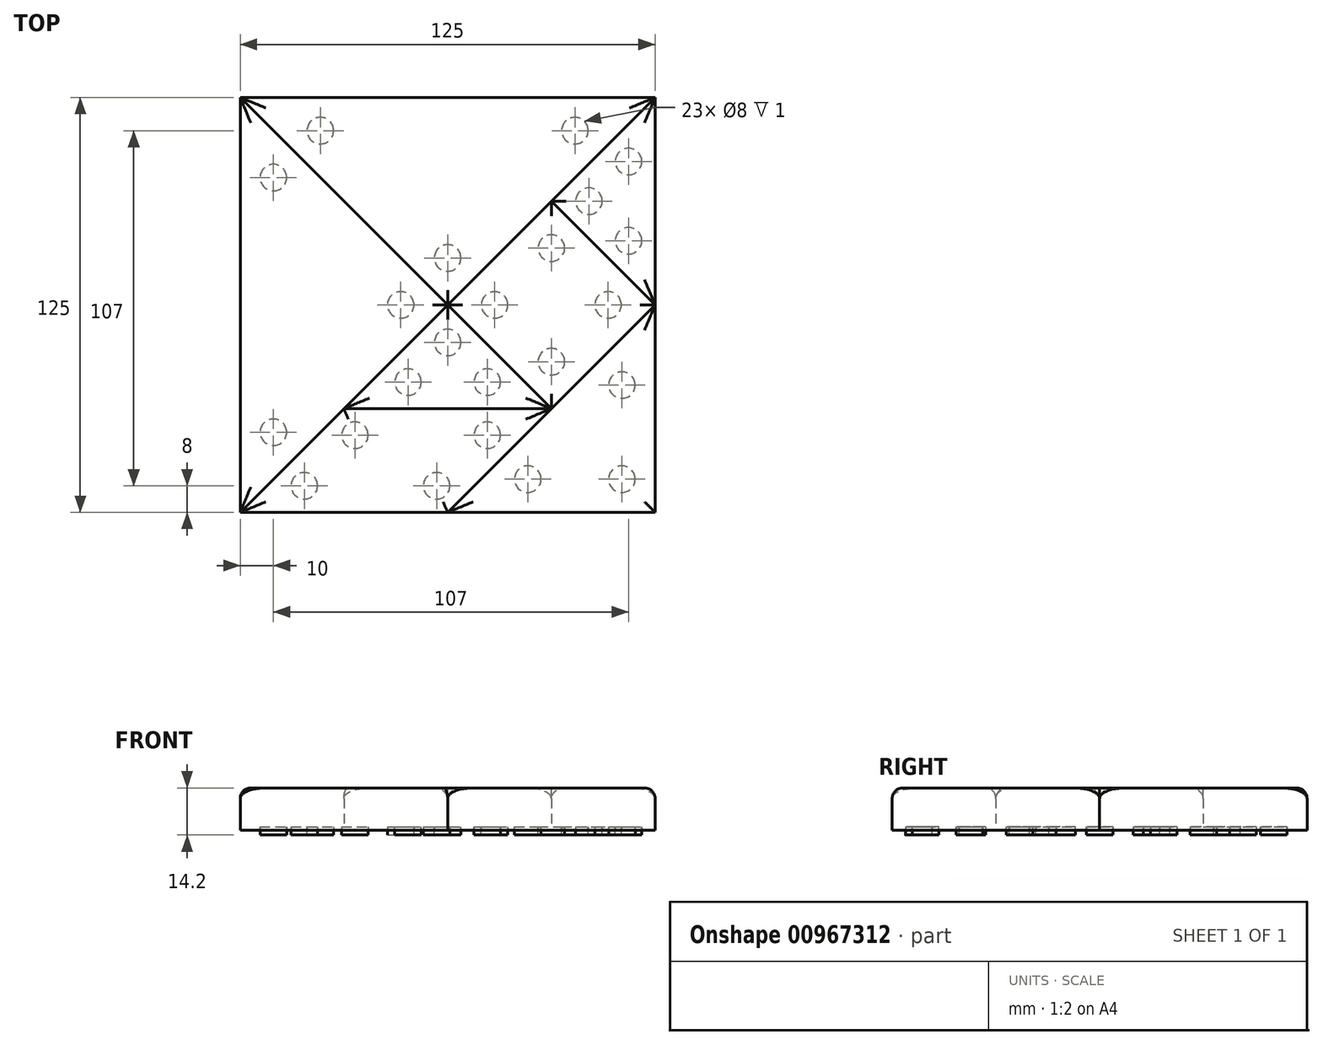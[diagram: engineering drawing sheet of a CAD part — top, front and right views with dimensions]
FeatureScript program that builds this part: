
annotation { "Feature Type Name" : "Feature", "Feature Type Description" : "" }
export const myFeature = defineFeature(function(context is Context, id is Id, definition is map)
    precondition{}
    {
        {
            var Q0;
            Q0=qCreatedBy(makeId("Top.planeOp"),FACE);
            var sketch = newSketch(context, id + "F0", { "sketchPlane" : qUnion([Q0])});
            skLineSegment(sketch, "E0.bottom", {"start": v(62.5, -62.5) * mm, "end": v(-62.5, -62.5) * mm});
            skLineSegment(sketch, "E0.top", {"start": v(62.5, 62.5) * mm, "end": v(-62.5, 62.5) * mm});
            skLineSegment(sketch, "E0.left", {"start": v(62.5, -62.5) * mm, "end": v(62.5, 62.5) * mm});
            skLineSegment(sketch, "E0.right", {"start": v(-62.5, -62.5) * mm, "end": v(-62.5, 62.5) * mm});
            skPoint(sketch, "E0.middle", {"position": v(0, 0) * mm});
            skLineSegment(sketch, "E1", {"start": v(62.5, 62.5) * mm, "end": v(-62.5, -62.5) * mm});
            skLineSegment(sketch, "E2", {"start": v(0, -62.5) * mm, "end": v(62.5, 0) * mm});
            skLineSegment(sketch, "E3", {"start": v(0, 0) * mm, "end": v(31.25, -31.25) * mm});
            skLineSegment(sketch, "E4", {"start": v(62.5, 0) * mm, "end": v(31.25, 31.25) * mm});
            skLineSegment(sketch, "E5", {"start": v(31.25, -31.25) * mm, "end": v(-31.25, -31.25) * mm});
            skLineSegment(sketch, "E6", {"start": v(0, 0) * mm, "end": v(-62.5, 62.5) * mm});
            skSolve(sketch);
        }
        {
            var Q0;
            {var subQ0=sQuery(id+"F0.wireOp",EDGE,"E0.right");Q0=makeQuery(id+"F0.imprint","IMPRINT",FACE,{"disambiguationData":[TD([[makeQuery(id+"F0.imprint","IMPRINT",EDGE,{"derivedFrom":subQ0}),-1.0]])]});}
            extrude(context, id + "F1", {"entities" : qUnion([Q0]), "depth" : 12.7 * mm, "offsetDistance" : 25.4 * mm});
        }
        {
            var Q0;
            {var subQ0=sQuery(id+"F0.wireOp",EDGE,"E0.top");Q0=makeQuery(id+"F0.imprint","IMPRINT",FACE,{"disambiguationData":[TD([[makeQuery(id+"F0.imprint","IMPRINT",EDGE,{"derivedFrom":subQ0}),1.0]])]});}
            extrude(context, id + "F2", {"entities" : qUnion([Q0]), "depth" : 12.7 * mm, "offsetDistance" : 25.4 * mm});
        }
        {
            var Q0;
            {var subQ5=sQuery(id+"F0.wireOp",EDGE,"E5");Q0=makeQuery(id+"F0.imprint","IMPRINT",FACE,{"disambiguationData":[TD([[makeQuery(id+"F0.imprint","IMPRINT",EDGE,{"derivedFrom":subQ5}),1.0]])]});}
            extrude(context, id + "F3", {"entities" : qUnion([Q0]), "depth" : 12.7 * mm, "offsetDistance" : 25.4 * mm});
        }
        {
            var Q0;
            {var subQ0=sQuery(id+"F0.wireOp",EDGE,"E3");Q0=makeQuery(id+"F0.imprint","IMPRINT",FACE,{"disambiguationData":[TD([[makeQuery(id+"F0.imprint","IMPRINT",EDGE,{"derivedFrom":subQ0}),-1.0]])]});}
            extrude(context, id + "F4", {"entities" : qUnion([Q0]), "depth" : 12.7 * mm, "offsetDistance" : 25.4 * mm});
        }
        {
            var Q0;
            {var subQ0=sQuery(id+"F0.wireOp",EDGE,"E3");Q0=makeQuery(id+"F0.imprint","IMPRINT",FACE,{"disambiguationData":[TD([[makeQuery(id+"F0.imprint","IMPRINT",EDGE,{"derivedFrom":subQ0}),1.0]])]});}
            extrude(context, id + "F5", {"entities" : qUnion([Q0]), "depth" : 12.7 * mm, "offsetDistance" : 25.4 * mm});
        }
        {
            var Q0;
            {var subQ0=sQuery(id+"F0.wireOp",EDGE,"E0.left");var subQ1=sQuery(id+"F0.wireOp",EDGE,"E0.bottom");var subQ2=makeQuery(id+"F0.imprint","INTERSECT",VERTEX,{"derivedFrom":[subQ1,subQ0]});Q0=makeQuery(id+"F0.imprint","IMPRINT",FACE,{"disambiguationData":[TD([[makeQuery(id+"F0.imprint","IMPRINT",EDGE,{"disambiguationData":[TD([[subQ2,-1.0]])],"derivedFrom":subQ1}),-1.0]])]});}
            extrude(context, id + "F6", {"entities" : qUnion([Q0]), "depth" : 12.7 * mm, "offsetDistance" : 25.4 * mm});
        }
        {
            var Q0;
            {var subQ3=sQuery(id+"F0.wireOp",EDGE,"E4");Q0=makeQuery(id+"F0.imprint","IMPRINT",FACE,{"disambiguationData":[TD([[makeQuery(id+"F0.imprint","IMPRINT",EDGE,{"derivedFrom":subQ3}),-1.0]])]});}
            extrude(context, id + "F7", {"entities" : qUnion([Q0]), "depth" : 12.7 * mm, "offsetDistance" : 25.4 * mm});
        }
        {
            var Q0;
            Q0=makeQuery(id+"F1.opExtrude","CAP_FACE",FACE,{"disambiguationData":[OSD([sQuery(id+"F0.wireOp",EDGE,"E0.right"),sQuery(id+"F0.wireOp",EDGE,"E1"),sQuery(id+"F0.wireOp",EDGE,"E6")])],"isStart":false});
            var Q1;
            Q1=makeQuery(id+"F2.opExtrude","CAP_FACE",FACE,{"disambiguationData":[OSD([sQuery(id+"F0.wireOp",EDGE,"E0.top"),sQuery(id+"F0.wireOp",EDGE,"E1"),sQuery(id+"F0.wireOp",EDGE,"E6")])],"isStart":false});
            var Q2;
            Q2=makeQuery(id+"F3.opExtrude","CAP_FACE",FACE,{"disambiguationData":[OSD([sQuery(id+"F0.wireOp",EDGE,"E0.bottom"),sQuery(id+"F0.wireOp",EDGE,"E1"),sQuery(id+"F0.wireOp",EDGE,"E2"),sQuery(id+"F0.wireOp",EDGE,"E5")])],"isStart":false});
            var Q3;
            Q3=makeQuery(id+"F4.opExtrude","CAP_FACE",FACE,{"disambiguationData":[OSD([sQuery(id+"F0.wireOp",EDGE,"E1"),sQuery(id+"F0.wireOp",EDGE,"E3"),sQuery(id+"F0.wireOp",EDGE,"E5")])],"isStart":false});
            var Q4;
            Q4=makeQuery(id+"F6.opExtrude","CAP_FACE",FACE,{"disambiguationData":[OSD([sQuery(id+"F0.wireOp",EDGE,"E0.bottom"),sQuery(id+"F0.wireOp",EDGE,"E0.left"),sQuery(id+"F0.wireOp",EDGE,"E2")])],"isStart":false});
            var Q5;
            Q5=makeQuery(id+"F5.opExtrude","CAP_FACE",FACE,{"disambiguationData":[OSD([sQuery(id+"F0.wireOp",EDGE,"E1"),sQuery(id+"F0.wireOp",EDGE,"E2"),sQuery(id+"F0.wireOp",EDGE,"E3"),sQuery(id+"F0.wireOp",EDGE,"E4")])],"isStart":false});
            var Q6;
            Q6=makeQuery(id+"F7.opExtrude","CAP_FACE",FACE,{"disambiguationData":[OSD([sQuery(id+"F0.wireOp",EDGE,"E0.left"),sQuery(id+"F0.wireOp",EDGE,"E1"),sQuery(id+"F0.wireOp",EDGE,"E4")])],"isStart":false});
            fillet(context, id + "F8", {"entities" : qUnion([Q0, Q1, Q2, Q3, Q4, Q5, Q6]), "radius" : 3.17 * mm, "tangentPropagation" : true, "allowEdgeOverflow" : false});
        }
        {
            var Q0;
            Q0=makeQuery(id+"F2.opExtrude","CAP_FACE",FACE,{"disambiguationData":[OSD([sQuery(id+"F0.wireOp",EDGE,"E0.top"),sQuery(id+"F0.wireOp",EDGE,"E1"),sQuery(id+"F0.wireOp",EDGE,"E6")])],"isStart":true});
            var sketch = newSketch(context, id + "F9", { "sketchPlane" : qUnion([Q0])});
            skCircle(sketch, "E7", {"center": v(0, -14.14) * mm, "radius": 4 * mm});
            skCircle(sketch, "E8", {"center": v(38.36, -52.5) * mm, "radius": 4 * mm});
            skCircle(sketch, "E9", {"center": v(-38.36, -52.5) * mm, "radius": 4 * mm});
            skSolve(sketch);
        }
        {
            var Q0;
            Q0=makeQuery(id+"F5.opExtrude","CAP_FACE",FACE,{"disambiguationData":[OSD([sQuery(id+"F0.wireOp",EDGE,"E1"),sQuery(id+"F0.wireOp",EDGE,"E2"),sQuery(id+"F0.wireOp",EDGE,"E3"),sQuery(id+"F0.wireOp",EDGE,"E4")])],"isStart":true});
            var sketch = newSketch(context, id + "F10", { "sketchPlane" : qUnion([Q0])});
            skCircle(sketch, "E10", {"center": v(48.36, 0) * mm, "radius": 4 * mm});
            skCircle(sketch, "E11", {"center": v(14.14, 0) * mm, "radius": 4 * mm});
            skCircle(sketch, "E12", {"center": v(31.25, 17.1) * mm, "radius": 4 * mm});
            skCircle(sketch, "E13", {"center": v(31.25, -17.1) * mm, "radius": 4 * mm});
            skSolve(sketch);
        }
        {
            var Q0;
            Q0=makeQuery(id+"F4.opExtrude","CAP_FACE",FACE,{"disambiguationData":[OSD([sQuery(id+"F0.wireOp",EDGE,"E1"),sQuery(id+"F0.wireOp",EDGE,"E3"),sQuery(id+"F0.wireOp",EDGE,"E5")])],"isStart":true});
            var sketch = newSketch(context, id + "F11", { "sketchPlane" : qUnion([Q0])});
            skCircle(sketch, "E14", {"center": v(0, 11.31) * mm, "radius": 4 * mm});
            skCircle(sketch, "E15", {"center": v(11.94, 23.25) * mm, "radius": 4 * mm});
            skCircle(sketch, "E16", {"center": v(-11.94, 23.25) * mm, "radius": 4 * mm});
            skSolve(sketch);
        }
        {
            var Q0;
            Q0=makeQuery(id+"F1.opExtrude","CAP_FACE",FACE,{"disambiguationData":[OSD([sQuery(id+"F0.wireOp",EDGE,"E0.right"),sQuery(id+"F0.wireOp",EDGE,"E1"),sQuery(id+"F0.wireOp",EDGE,"E6")])],"isStart":true});
            var sketch = newSketch(context, id + "F12", { "sketchPlane" : qUnion([Q0])});
            skCircle(sketch, "E17", {"center": v(-14.14, 0) * mm, "radius": 4 * mm});
            skCircle(sketch, "E18", {"center": v(-52.5, -38.36) * mm, "radius": 4 * mm});
            skCircle(sketch, "E19", {"center": v(-52.5, 38.36) * mm, "radius": 4 * mm});
            skSolve(sketch);
        }
        {
            var Q0;
            Q0=makeQuery(id+"F6.opExtrude","CAP_FACE",FACE,{"disambiguationData":[OSD([sQuery(id+"F0.wireOp",EDGE,"E0.bottom"),sQuery(id+"F0.wireOp",EDGE,"E0.left"),sQuery(id+"F0.wireOp",EDGE,"E2")])],"isStart":true});
            var sketch = newSketch(context, id + "F13", { "sketchPlane" : qUnion([Q0])});
            skCircle(sketch, "E20", {"center": v(52.5, 52.5) * mm, "radius": 4 * mm});
            skCircle(sketch, "E21", {"center": v(52.5, 24.14) * mm, "radius": 4 * mm});
            skCircle(sketch, "E22", {"center": v(24.14, 52.5) * mm, "radius": 4 * mm});
            skSolve(sketch);
        }
        {
            var Q0;
            Q0=makeQuery(id+"F3.opExtrude","CAP_FACE",FACE,{"disambiguationData":[OSD([sQuery(id+"F0.wireOp",EDGE,"E0.bottom"),sQuery(id+"F0.wireOp",EDGE,"E1"),sQuery(id+"F0.wireOp",EDGE,"E2"),sQuery(id+"F0.wireOp",EDGE,"E5")])],"isStart":true});
            var sketch = newSketch(context, id + "F14", { "sketchPlane" : qUnion([Q0])});
            skCircle(sketch, "E23", {"center": v(-3.31, 54.5) * mm, "radius": 4 * mm});
            skCircle(sketch, "E24", {"center": v(11.94, 39.25) * mm, "radius": 4 * mm});
            skCircle(sketch, "E25", {"center": v(-27.94, 39.25) * mm, "radius": 4 * mm});
            skCircle(sketch, "E26", {"center": v(-43.19, 54.5) * mm, "radius": 4 * mm});
            skSolve(sketch);
        }
        {
            var Q0;
            Q0=makeQuery(id+"F7.opExtrude","CAP_FACE",FACE,{"disambiguationData":[OSD([sQuery(id+"F0.wireOp",EDGE,"E0.left"),sQuery(id+"F0.wireOp",EDGE,"E1"),sQuery(id+"F0.wireOp",EDGE,"E4")])],"isStart":true});
            var sketch = newSketch(context, id + "F15", { "sketchPlane" : qUnion([Q0])});
            skCircle(sketch, "E27", {"center": v(54.5, -19.31) * mm, "radius": 4 * mm});
            skCircle(sketch, "E28", {"center": v(42.56, -31.25) * mm, "radius": 4 * mm});
            skCircle(sketch, "E29", {"center": v(54.5, -43.19) * mm, "radius": 4 * mm});
            skSolve(sketch);
        }
        {
            var Q0;
            Q0=makeQuery(id+"F12.imprint","IMPRINT",FACE,{"disambiguationData":[TD([[makeQuery(id+"F12.imprint","IMPRINT",EDGE,{"derivedFrom":sQuery(id+"F12.wireOp",EDGE,"E19")}),1.0]])]});
            var Q1;
            Q1=makeQuery(id+"F12.imprint","IMPRINT",FACE,{"disambiguationData":[TD([[makeQuery(id+"F12.imprint","IMPRINT",EDGE,{"derivedFrom":sQuery(id+"F12.wireOp",EDGE,"E17")}),1.0]])]});
            var Q2;
            Q2=makeQuery(id+"F12.imprint","IMPRINT",FACE,{"disambiguationData":[TD([[makeQuery(id+"F12.imprint","IMPRINT",EDGE,{"derivedFrom":sQuery(id+"F12.wireOp",EDGE,"E18")}),1.0]])]});
            extrude(context, id + "F16", {"entities" : qUnion([Q0, Q1, Q2]), "operationType" : NewBodyOperationType.REMOVE, "oppositeDirection" : true, "depth" : 1 * mm, "offsetDistance" : 25 * mm});
        }
        {
            var Q0;
            Q0=makeQuery(id+"F9.imprint","IMPRINT",FACE,{"disambiguationData":[TD([[makeQuery(id+"F9.imprint","IMPRINT",EDGE,{"derivedFrom":sQuery(id+"F9.wireOp",EDGE,"E7")}),1.0]])]});
            var Q1;
            Q1=makeQuery(id+"F9.imprint","IMPRINT",FACE,{"disambiguationData":[TD([[makeQuery(id+"F9.imprint","IMPRINT",EDGE,{"derivedFrom":sQuery(id+"F9.wireOp",EDGE,"E9")}),1.0]])]});
            var Q2;
            Q2=makeQuery(id+"F9.imprint","IMPRINT",FACE,{"disambiguationData":[TD([[makeQuery(id+"F9.imprint","IMPRINT",EDGE,{"derivedFrom":sQuery(id+"F9.wireOp",EDGE,"E8")}),1.0]])]});
            extrude(context, id + "F17", {"entities" : qUnion([Q0, Q1, Q2]), "operationType" : NewBodyOperationType.REMOVE, "oppositeDirection" : true, "depth" : 1 * mm, "offsetDistance" : 25 * mm});
        }
        {
            var Q0;
            Q0=makeQuery(id+"F15.imprint","IMPRINT",FACE,{"disambiguationData":[TD([[makeQuery(id+"F15.imprint","IMPRINT",EDGE,{"derivedFrom":sQuery(id+"F15.wireOp",EDGE,"E28")}),1.0]])]});
            var Q1;
            Q1=makeQuery(id+"F15.imprint","IMPRINT",FACE,{"disambiguationData":[TD([[makeQuery(id+"F15.imprint","IMPRINT",EDGE,{"derivedFrom":sQuery(id+"F15.wireOp",EDGE,"E27")}),1.0]])]});
            var Q2;
            Q2=makeQuery(id+"F15.imprint","IMPRINT",FACE,{"disambiguationData":[TD([[makeQuery(id+"F15.imprint","IMPRINT",EDGE,{"derivedFrom":sQuery(id+"F15.wireOp",EDGE,"E29")}),1.0]])]});
            extrude(context, id + "F18", {"entities" : qUnion([Q0, Q1, Q2]), "operationType" : NewBodyOperationType.REMOVE, "oppositeDirection" : true, "depth" : 1 * mm, "offsetDistance" : 25 * mm});
        }
        {
            var Q0;
            Q0=makeQuery(id+"F10.imprint","IMPRINT",FACE,{"disambiguationData":[TD([[makeQuery(id+"F10.imprint","IMPRINT",EDGE,{"derivedFrom":sQuery(id+"F10.wireOp",EDGE,"E11")}),1.0]])]});
            var Q1;
            Q1=makeQuery(id+"F10.imprint","IMPRINT",FACE,{"disambiguationData":[TD([[makeQuery(id+"F10.imprint","IMPRINT",EDGE,{"derivedFrom":sQuery(id+"F10.wireOp",EDGE,"E12")}),1.0]])]});
            var Q2;
            Q2=makeQuery(id+"F10.imprint","IMPRINT",FACE,{"disambiguationData":[TD([[makeQuery(id+"F10.imprint","IMPRINT",EDGE,{"derivedFrom":sQuery(id+"F10.wireOp",EDGE,"E10")}),1.0]])]});
            var Q3;
            Q3=makeQuery(id+"F10.imprint","IMPRINT",FACE,{"disambiguationData":[TD([[makeQuery(id+"F10.imprint","IMPRINT",EDGE,{"derivedFrom":sQuery(id+"F10.wireOp",EDGE,"E13")}),1.0]])]});
            extrude(context, id + "F19", {"entities" : qUnion([Q0, Q1, Q2, Q3]), "operationType" : NewBodyOperationType.REMOVE, "oppositeDirection" : true, "depth" : 1 * mm, "offsetDistance" : 25 * mm});
        }
        {
            var Q0;
            Q0=makeQuery(id+"F11.imprint","IMPRINT",FACE,{"disambiguationData":[TD([[makeQuery(id+"F11.imprint","IMPRINT",EDGE,{"derivedFrom":sQuery(id+"F11.wireOp",EDGE,"E16")}),1.0]])]});
            var Q1;
            Q1=makeQuery(id+"F11.imprint","IMPRINT",FACE,{"disambiguationData":[TD([[makeQuery(id+"F11.imprint","IMPRINT",EDGE,{"derivedFrom":sQuery(id+"F11.wireOp",EDGE,"E14")}),1.0]])]});
            var Q2;
            Q2=makeQuery(id+"F11.imprint","IMPRINT",FACE,{"disambiguationData":[TD([[makeQuery(id+"F11.imprint","IMPRINT",EDGE,{"derivedFrom":sQuery(id+"F11.wireOp",EDGE,"E15")}),1.0]])]});
            extrude(context, id + "F20", {"entities" : qUnion([Q0, Q1, Q2]), "operationType" : NewBodyOperationType.REMOVE, "oppositeDirection" : true, "depth" : 1 * mm, "offsetDistance" : 25 * mm});
        }
        {
            var Q0;
            Q0=makeQuery(id+"F14.imprint","IMPRINT",FACE,{"disambiguationData":[TD([[makeQuery(id+"F14.imprint","IMPRINT",EDGE,{"derivedFrom":sQuery(id+"F14.wireOp",EDGE,"E25")}),1.0]])]});
            var Q1;
            Q1=makeQuery(id+"F14.imprint","IMPRINT",FACE,{"disambiguationData":[TD([[makeQuery(id+"F14.imprint","IMPRINT",EDGE,{"derivedFrom":sQuery(id+"F14.wireOp",EDGE,"E26")}),1.0]])]});
            var Q2;
            Q2=makeQuery(id+"F14.imprint","IMPRINT",FACE,{"disambiguationData":[TD([[makeQuery(id+"F14.imprint","IMPRINT",EDGE,{"derivedFrom":sQuery(id+"F14.wireOp",EDGE,"E23")}),1.0]])]});
            var Q3;
            Q3=makeQuery(id+"F14.imprint","IMPRINT",FACE,{"disambiguationData":[TD([[makeQuery(id+"F14.imprint","IMPRINT",EDGE,{"derivedFrom":sQuery(id+"F14.wireOp",EDGE,"E24")}),1.0]])]});
            extrude(context, id + "F21", {"entities" : qUnion([Q0, Q1, Q2, Q3]), "operationType" : NewBodyOperationType.REMOVE, "oppositeDirection" : true, "depth" : 1 * mm, "offsetDistance" : 25 * mm});
        }
        {
            var Q0;
            Q0=makeQuery(id+"F13.imprint","IMPRINT",FACE,{"disambiguationData":[TD([[makeQuery(id+"F13.imprint","IMPRINT",EDGE,{"derivedFrom":sQuery(id+"F13.wireOp",EDGE,"E22")}),1.0]])]});
            var Q1;
            Q1=makeQuery(id+"F13.imprint","IMPRINT",FACE,{"disambiguationData":[TD([[makeQuery(id+"F13.imprint","IMPRINT",EDGE,{"derivedFrom":sQuery(id+"F13.wireOp",EDGE,"E20")}),1.0]])]});
            var Q2;
            Q2=makeQuery(id+"F13.imprint","IMPRINT",FACE,{"disambiguationData":[TD([[makeQuery(id+"F13.imprint","IMPRINT",EDGE,{"derivedFrom":sQuery(id+"F13.wireOp",EDGE,"E21")}),1.0]])]});
            extrude(context, id + "F22", {"entities" : qUnion([Q0, Q1, Q2]), "operationType" : NewBodyOperationType.REMOVE, "oppositeDirection" : true, "depth" : 1 * mm, "offsetDistance" : 25 * mm});
        }
        {
            var Q0;
            Q0=makeQuery(id+"F16.boolean.opBoolean","COPY",FACE,{"derivedFrom":makeQuery(id+"F16.opExtrude","CAP_FACE",FACE,{"disambiguationData":[OSD([sQuery(id+"F12.wireOp",EDGE,"E19")])],"isStart":false})});
            var Q1;
            Q1=makeQuery(id+"F16.boolean.opBoolean","COPY",FACE,{"derivedFrom":makeQuery(id+"F16.opExtrude","CAP_FACE",FACE,{"disambiguationData":[OSD([sQuery(id+"F12.wireOp",EDGE,"E17")])],"isStart":false})});
            var Q2;
            Q2=makeQuery(id+"F16.boolean.opBoolean","COPY",FACE,{"derivedFrom":makeQuery(id+"F16.opExtrude","CAP_FACE",FACE,{"disambiguationData":[OSD([sQuery(id+"F12.wireOp",EDGE,"E18")])],"isStart":false})});
            var Q3;
            Q3=makeQuery(id+"F17.boolean.opBoolean","COPY",FACE,{"derivedFrom":makeQuery(id+"F17.opExtrude","CAP_FACE",FACE,{"disambiguationData":[OSD([sQuery(id+"F9.wireOp",EDGE,"E9")])],"isStart":false})});
            var Q4;
            Q4=makeQuery(id+"F17.boolean.opBoolean","COPY",FACE,{"derivedFrom":makeQuery(id+"F17.opExtrude","CAP_FACE",FACE,{"disambiguationData":[OSD([sQuery(id+"F9.wireOp",EDGE,"E7")])],"isStart":false})});
            var Q5;
            Q5=makeQuery(id+"F17.boolean.opBoolean","COPY",FACE,{"derivedFrom":makeQuery(id+"F17.opExtrude","CAP_FACE",FACE,{"disambiguationData":[OSD([sQuery(id+"F9.wireOp",EDGE,"E8")])],"isStart":false})});
            var Q6;
            Q6=makeQuery(id+"F18.boolean.opBoolean","COPY",FACE,{"derivedFrom":makeQuery(id+"F18.opExtrude","CAP_FACE",FACE,{"disambiguationData":[OSD([sQuery(id+"F15.wireOp",EDGE,"E29")])],"isStart":false})});
            var Q7;
            Q7=makeQuery(id+"F18.boolean.opBoolean","COPY",FACE,{"derivedFrom":makeQuery(id+"F18.opExtrude","CAP_FACE",FACE,{"disambiguationData":[OSD([sQuery(id+"F15.wireOp",EDGE,"E28")])],"isStart":false})});
            var Q8;
            Q8=makeQuery(id+"F18.boolean.opBoolean","COPY",FACE,{"derivedFrom":makeQuery(id+"F18.opExtrude","CAP_FACE",FACE,{"disambiguationData":[OSD([sQuery(id+"F15.wireOp",EDGE,"E27")])],"isStart":false})});
            var Q9;
            Q9=makeQuery(id+"F19.boolean.opBoolean","COPY",FACE,{"derivedFrom":makeQuery(id+"F19.opExtrude","CAP_FACE",FACE,{"disambiguationData":[OSD([sQuery(id+"F10.wireOp",EDGE,"E10")])],"isStart":false})});
            var Q10;
            Q10=makeQuery(id+"F19.boolean.opBoolean","COPY",FACE,{"derivedFrom":makeQuery(id+"F19.opExtrude","CAP_FACE",FACE,{"disambiguationData":[OSD([sQuery(id+"F10.wireOp",EDGE,"E13")])],"isStart":false})});
            var Q11;
            Q11=makeQuery(id+"F19.boolean.opBoolean","COPY",FACE,{"derivedFrom":makeQuery(id+"F19.opExtrude","CAP_FACE",FACE,{"disambiguationData":[OSD([sQuery(id+"F10.wireOp",EDGE,"E11")])],"isStart":false})});
            var Q12;
            Q12=makeQuery(id+"F19.boolean.opBoolean","COPY",FACE,{"derivedFrom":makeQuery(id+"F19.opExtrude","CAP_FACE",FACE,{"disambiguationData":[OSD([sQuery(id+"F10.wireOp",EDGE,"E12")])],"isStart":false})});
            var Q13;
            Q13=makeQuery(id+"F22.boolean.opBoolean","COPY",FACE,{"derivedFrom":makeQuery(id+"F22.opExtrude","CAP_FACE",FACE,{"disambiguationData":[OSD([sQuery(id+"F13.wireOp",EDGE,"E21")])],"isStart":false})});
            var Q14;
            Q14=makeQuery(id+"F22.boolean.opBoolean","COPY",FACE,{"derivedFrom":makeQuery(id+"F22.opExtrude","CAP_FACE",FACE,{"disambiguationData":[OSD([sQuery(id+"F13.wireOp",EDGE,"E20")])],"isStart":false})});
            var Q15;
            Q15=makeQuery(id+"F22.boolean.opBoolean","COPY",FACE,{"derivedFrom":makeQuery(id+"F22.opExtrude","CAP_FACE",FACE,{"disambiguationData":[OSD([sQuery(id+"F13.wireOp",EDGE,"E22")])],"isStart":false})});
            var Q16;
            Q16=makeQuery(id+"F21.boolean.opBoolean","COPY",FACE,{"derivedFrom":makeQuery(id+"F21.opExtrude","CAP_FACE",FACE,{"disambiguationData":[OSD([sQuery(id+"F14.wireOp",EDGE,"E24")])],"isStart":false})});
            var Q17;
            Q17=makeQuery(id+"F21.boolean.opBoolean","COPY",FACE,{"derivedFrom":makeQuery(id+"F21.opExtrude","CAP_FACE",FACE,{"disambiguationData":[OSD([sQuery(id+"F14.wireOp",EDGE,"E23")])],"isStart":false})});
            var Q18;
            Q18=makeQuery(id+"F20.boolean.opBoolean","COPY",FACE,{"derivedFrom":makeQuery(id+"F20.opExtrude","CAP_FACE",FACE,{"disambiguationData":[OSD([sQuery(id+"F11.wireOp",EDGE,"E15")])],"isStart":false})});
            var Q19;
            Q19=makeQuery(id+"F20.boolean.opBoolean","COPY",FACE,{"derivedFrom":makeQuery(id+"F20.opExtrude","CAP_FACE",FACE,{"disambiguationData":[OSD([sQuery(id+"F11.wireOp",EDGE,"E14")])],"isStart":false})});
            var Q20;
            Q20=makeQuery(id+"F20.boolean.opBoolean","COPY",FACE,{"derivedFrom":makeQuery(id+"F20.opExtrude","CAP_FACE",FACE,{"disambiguationData":[OSD([sQuery(id+"F11.wireOp",EDGE,"E16")])],"isStart":false})});
            var Q21;
            Q21=makeQuery(id+"F21.boolean.opBoolean","COPY",FACE,{"derivedFrom":makeQuery(id+"F21.opExtrude","CAP_FACE",FACE,{"disambiguationData":[OSD([sQuery(id+"F14.wireOp",EDGE,"E25")])],"isStart":false})});
            var Q22;
            Q22=makeQuery(id+"F21.boolean.opBoolean","COPY",FACE,{"derivedFrom":makeQuery(id+"F21.opExtrude","CAP_FACE",FACE,{"disambiguationData":[OSD([sQuery(id+"F14.wireOp",EDGE,"E26")])],"isStart":false})});
            extrude(context, id + "F23", {"entities" : qUnion([Q0, Q1, Q2, Q3, Q4, Q5, Q6, Q7, Q8, Q9, Q10, Q11, Q12, Q13, Q14, Q15, Q16, Q17, Q18, Q19, Q20, Q21, Q22]), "depth" : 2.5 * mm, "offsetDistance" : 25 * mm});
        }
    });
